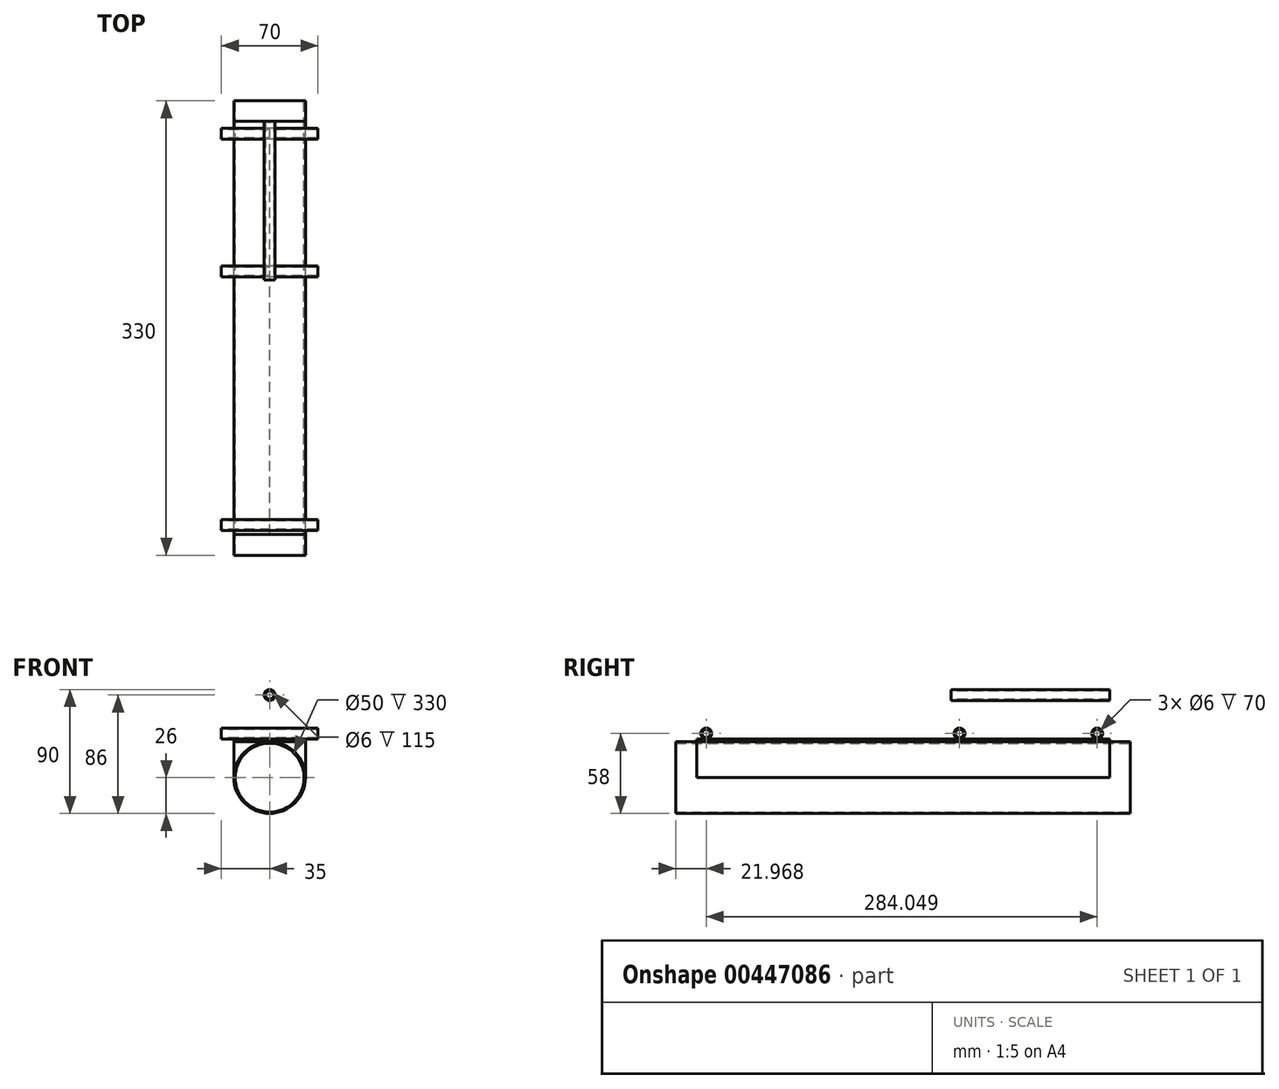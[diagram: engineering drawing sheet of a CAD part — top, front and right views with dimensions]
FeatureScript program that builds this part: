
annotation { "Feature Type Name" : "Feature", "Feature Type Description" : "" }
export const myFeature = defineFeature(function(context is Context, id is Id, definition is map)
    precondition{}
    {
        {
            var Q0;
            Q0=qCreatedBy(makeId("Front.planeOp"),FACE);
            var sketch = newSketch(context, id + "F0", { "sketchPlane" : qUnion([Q0])});
            skCircle(sketch, "E0", {"center": v(0, 0) * mm, "radius": 26 * mm});
            skCircle(sketch, "E1", {"center": v(0, 0) * mm, "radius": 25 * mm});
            skLineSegment(sketch, "E2.bottom", {"start": v(-26, 28) * mm, "end": v(26, 28) * mm});
            skLineSegment(sketch, "E2.top", {"start": v(-26, 26) * mm, "end": v(26, 26) * mm});
            skLineSegment(sketch, "E2.left", {"start": v(-26, 28) * mm, "end": v(-26, 26) * mm});
            skLineSegment(sketch, "E2.right", {"start": v(26, 28) * mm, "end": v(26, 26) * mm});
            skLineSegment(sketch, "E3.top", {"start": v(-26, 0) * mm, "end": v(-25, 0) * mm});
            skLineSegment(sketch, "E3.left", {"start": v(-26, 26) * mm, "end": v(-26, 0) * mm});
            skLineSegment(sketch, "E3.right", {"start": v(26, 26) * mm, "end": v(26, 0) * mm});
            skLineSegment(sketch, "E4.trimOffspring", {"start": v(25, 0) * mm, "end": v(26, 0) * mm});
            skSolve(sketch);
        }
        {
            var Q0;
            {var subQ0=sQuery(id+"F0.wireOp",EDGE,"E3.top");Q0=makeQuery(id+"F0.imprint","IMPRINT",FACE,{"disambiguationData":[TD([[makeQuery(id+"F0.imprint","IMPRINT",EDGE,{"derivedFrom":subQ0}),1.0]])]});}
            var Q1;
            {var subQ0=sQuery(id+"F0.wireOp",EDGE,"E3.top");Q1=makeQuery(id+"F0.imprint","IMPRINT",FACE,{"disambiguationData":[TD([[makeQuery(id+"F0.imprint","IMPRINT",EDGE,{"derivedFrom":subQ0}),-1.0]])]});}
            extrude(context, id + "F1", {"entities" : qUnion([Q0, Q1]), "endBound" : BoundingType.SYMMETRIC, "depth" : 330 * mm});
        }
        {
            var Q0;
            Q0=makeQuery(id+"F0.imprint","IMPRINT",FACE,{"disambiguationData":[TD([[makeQuery(id+"F0.imprint","IMPRINT",EDGE,{"derivedFrom":sQuery(id+"F0.wireOp",EDGE,"E2.bottom")}),-1.0]])]});
            extrude(context, id + "F2", {"entities" : qUnion([Q0]), "operationType" : NewBodyOperationType.ADD, "endBound" : BoundingType.SYMMETRIC, "depth" : 300 * mm});
        }
        {
            var Q0;
            {var subQ0=sQuery(id+"F0.wireOp",EDGE,"E3.right");Q0=makeQuery(id+"F0.imprint","IMPRINT",FACE,{"disambiguationData":[TD([[makeQuery(id+"F0.imprint","IMPRINT",EDGE,{"derivedFrom":subQ0}),-1.0]])]});}
            var Q1;
            {var subQ0=sQuery(id+"F0.wireOp",EDGE,"E3.left");Q1=makeQuery(id+"F0.imprint","IMPRINT",FACE,{"disambiguationData":[TD([[makeQuery(id+"F0.imprint","IMPRINT",EDGE,{"derivedFrom":subQ0}),1.0]])]});}
            extrude(context, id + "F3", {"entities" : qUnion([Q0, Q1]), "endBound" : BoundingType.SYMMETRIC, "depth" : 300 * mm});
        }
        {
            var Q0;
            Q0=qCreatedBy(makeId("Front.planeOp"),FACE);
            var sketch = newSketch(context, id + "F4", { "sketchPlane" : qUnion([Q0])});
            skCircle(sketch, "E5", {"center": v(0, 60) * mm, "radius": 4 * mm});
            skCircle(sketch, "E6", {"center": v(0, 60) * mm, "radius": 3 * mm});
            skLineSegment(sketch, "E7", {"start": v(0, 60) * mm, "end": v(0, 0) * mm, "construction": true});
            skCircle(sketch, "E8", {"center": v(0, 60) * mm, "radius": 2 * mm});
            skSolve(sketch);
        }
        {
            var Q0;
            Q0=makeQuery(id+"F4.imprint","IMPRINT",FACE,{"disambiguationData":[TD([[makeQuery(id+"F4.imprint","IMPRINT",EDGE,{"derivedFrom":sQuery(id+"F4.wireOp",EDGE,"E5")}),1.0]])]});
            extrude(context, id + "F5", {"entities" : qUnion([Q0]), "oppositeDirection" : true, "depth" : 150 * mm, "hasSecondDirection" : true, "secondDirectionOppositeDirection" : true, "secondDirectionDepth" : 35 * mm});
        }
        {
            var Q0;
            Q0=qCreatedBy(makeId("Right.planeOp"),FACE);
            var sketch = newSketch(context, id + "F6", { "sketchPlane" : qUnion([Q0])});
            skCircle(sketch, "E9", {"center": v(-143.03, 32) * mm, "radius": 4 * mm});
            skCircle(sketch, "E10", {"center": v(141.02, 32) * mm, "radius": 4 * mm});
            skCircle(sketch, "E11", {"center": v(41.02, 32) * mm, "radius": 4 * mm});
            skCircle(sketch, "E12", {"center": v(-143.03, 32) * mm, "radius": 3 * mm});
            skCircle(sketch, "E13", {"center": v(41.02, 32) * mm, "radius": 3 * mm});
            skCircle(sketch, "E14", {"center": v(141.02, 32) * mm, "radius": 3 * mm});
            skLineSegment(sketch, "E15", {"start": v(41.02, 32) * mm, "end": v(141.02, 32) * mm, "construction": true});
            skLineSegment(sketch, "E16", {"start": v(-143.03, 32) * mm, "end": v(41.02, 32) * mm, "construction": true});
            skPoint(sketch, "E17", {"position": v(-150, 0) * mm});
            skPoint(sketch, "E18", {"position": v(-142.95, 36) * mm});
            skPoint(sketch, "E19", {"position": v(-46.4, 0) * mm});
            skPoint(sketch, "E20", {"position": v(40.93, 36) * mm});
            skPoint(sketch, "E21", {"position": v(95.5, 0) * mm});
            skPoint(sketch, "E22", {"position": v(140.93, 36) * mm});
            skSolve(sketch);
        }
        {
            var Q0;
            Q0 = qSketchRegion(id + "F6", true);
            extrude(context, id + "F7", {"entities" : qUnion([Q0]), "operationType" : NewBodyOperationType.ADD, "endBound" : BoundingType.SYMMETRIC, "depth" : 70 * mm});
        }
    });
